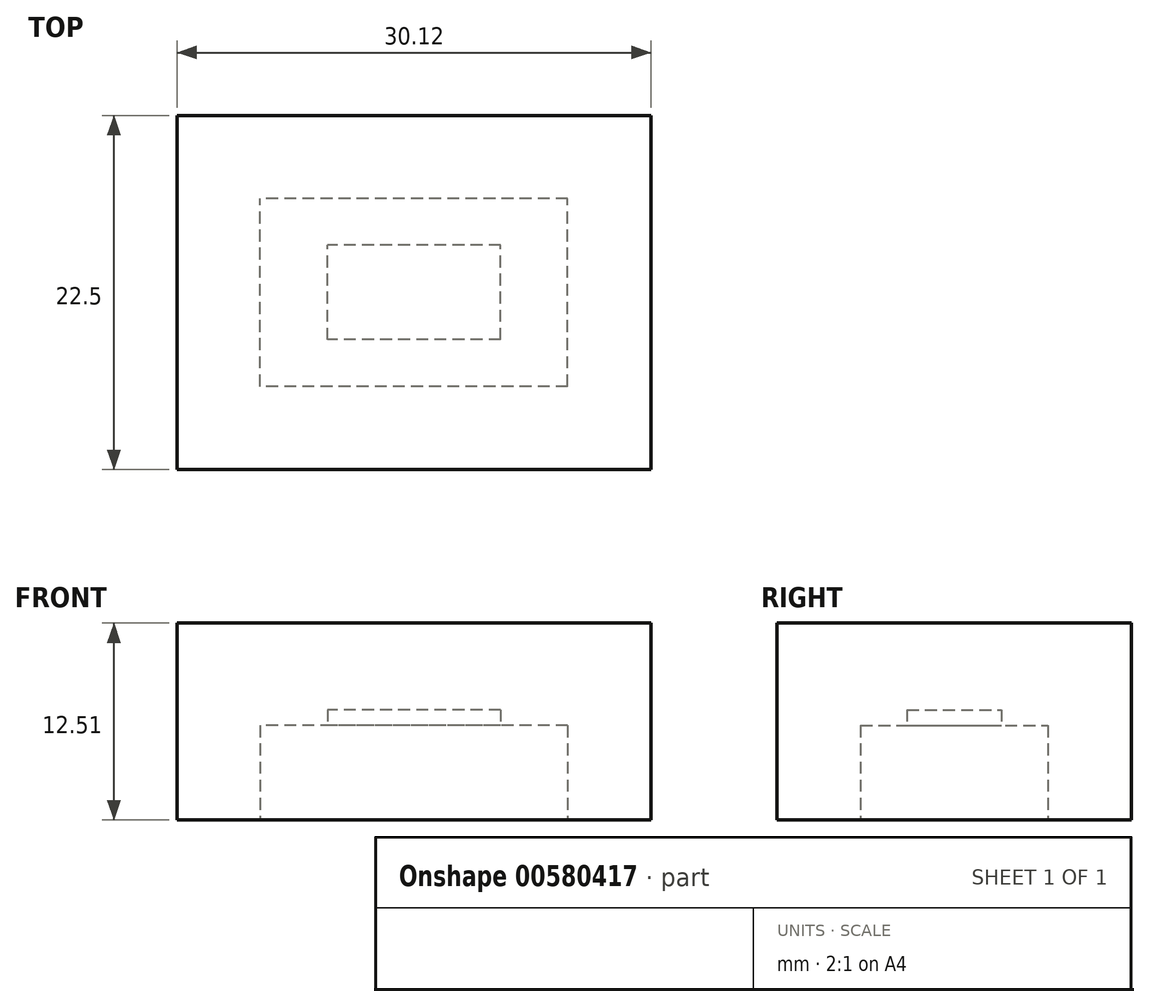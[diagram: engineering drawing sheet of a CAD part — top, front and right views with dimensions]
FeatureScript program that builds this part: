
annotation { "Feature Type Name" : "Feature", "Feature Type Description" : "" }
export const myFeature = defineFeature(function(context is Context, id is Id, definition is map)
    precondition{}
    {
        {
            var Q0;
            Q0=qCreatedBy(makeId("Top.planeOp"),FACE);
            var sketch = newSketch(context, id + "F0", { "sketchPlane" : qUnion([Q0])});
            skLineSegment(sketch, "E0.bottom", {"start": v(15.06, -11.25) * mm, "end": v(-15.06, -11.25) * mm});
            skLineSegment(sketch, "E0.top", {"start": v(15.06, 11.25) * mm, "end": v(-15.06, 11.25) * mm});
            skLineSegment(sketch, "E0.left", {"start": v(15.06, -11.25) * mm, "end": v(15.06, 11.25) * mm});
            skLineSegment(sketch, "E0.right", {"start": v(-15.06, -11.25) * mm, "end": v(-15.06, 11.25) * mm});
            skPoint(sketch, "E0.middle", {"position": v(0, 0) * mm});
            skSolve(sketch);
        }
        {
            var Q0;
            Q0 = qSketchRegion(id + "F0", true);
            extrude(context, id + "F1", {"entities" : qUnion([Q0]), "oppositeDirection" : true, "depth" : 11 * mm, "offsetDistance" : 25.4 * mm});
        }
        {
            var Q0;
            Q0=makeQuery(id+"F1.opExtrude","CAP_FACE",FACE,{"disambiguationData":[OSD([sQuery(id+"F0.wireOp",EDGE,"E0.bottom"),sQuery(id+"F0.wireOp",EDGE,"E0.top"),sQuery(id+"F0.wireOp",EDGE,"E0.left"),sQuery(id+"F0.wireOp",EDGE,"E0.right")])],"isStart":false});
            var sketch = newSketch(context, id + "F2", { "sketchPlane" : qUnion([Q0])});
            skLineSegment(sketch, "E1.bottom", {"start": v(9.77, 5.96) * mm, "end": v(-9.77, 5.95) * mm});
            skLineSegment(sketch, "E1.top", {"start": v(9.77, -5.95) * mm, "end": v(-9.77, -5.96) * mm});
            skLineSegment(sketch, "E1.left", {"start": v(9.77, 5.96) * mm, "end": v(9.77, -5.95) * mm});
            skLineSegment(sketch, "E1.right", {"start": v(-9.77, 5.95) * mm, "end": v(-9.77, -5.96) * mm});
            skPoint(sketch, "E1.middle", {"position": v(0, 0) * mm});
            skSolve(sketch);
        }
        {
            var Q0;
            Q0 = qSketchRegion(id + "F2", true);
            extrude(context, id + "F3", {"entities" : qUnion([Q0]), "operationType" : NewBodyOperationType.REMOVE, "oppositeDirection" : true, "depth" : 6 * mm, "offsetDistance" : 25.4 * mm});
        }
        {
            var Q0;
            Q0=makeQuery(id+"F3.boolean.opBoolean","COPY",FACE,{"derivedFrom":makeQuery(id+"F3.opExtrude","CAP_FACE",FACE,{"disambiguationData":[OSD([sQuery(id+"F2.wireOp",EDGE,"E1.bottom"),sQuery(id+"F2.wireOp",EDGE,"E1.top"),sQuery(id+"F2.wireOp",EDGE,"E1.left"),sQuery(id+"F2.wireOp",EDGE,"E1.right")])],"isStart":false})});
            var sketch = newSketch(context, id + "F4", { "sketchPlane" : qUnion([Q0])});
            skLineSegment(sketch, "E2.bottom", {"start": v(5.5, 3) * mm, "end": v(-5.5, 3) * mm});
            skLineSegment(sketch, "E2.top", {"start": v(5.5, -3) * mm, "end": v(-5.5, -3) * mm});
            skLineSegment(sketch, "E2.left", {"start": v(5.5, 3) * mm, "end": v(5.5, -3) * mm});
            skLineSegment(sketch, "E2.right", {"start": v(-5.5, 3) * mm, "end": v(-5.5, -3) * mm});
            skPoint(sketch, "E2.middle", {"position": v(0, 0) * mm});
            skSolve(sketch);
        }
        {
            var Q0;
            Q0 = qSketchRegion(id + "F4", true);
            extrude(context, id + "F5", {"entities" : qUnion([Q0]), "operationType" : NewBodyOperationType.REMOVE, "oppositeDirection" : true, "depth" : 1 * mm, "offsetDistance" : 25.4 * mm});
        }
        {
            var Q0;
            Q0=makeQuery(id+"F1.opExtrude","CAP_FACE",FACE,{"disambiguationData":[OSD([sQuery(id+"F0.wireOp",EDGE,"E0.bottom"),sQuery(id+"F0.wireOp",EDGE,"E0.top"),sQuery(id+"F0.wireOp",EDGE,"E0.left"),sQuery(id+"F0.wireOp",EDGE,"E0.right")])],"isStart":true});
            extrude(context, id + "F6", {"entities" : qUnion([Q0]), "operationType" : NewBodyOperationType.ADD, "depth" : 1.5 * mm, "offsetDistance" : 25.4 * mm});
        }
    });
